SOLIDWORKS PART (.sldprt)
format: sldprt  version: not decoded by parser v0  size: 134,656 bytes
history: native  units: mm
features: plane x3, sketch x3, mirror x2, cut_extrude x2, material x1, extrude x1, fillet x1 (+13 scaffold rows collapsed)
feature tree (26):
  scaffold x13  (default folders/planes/origin — collapsed)
  material  "Material <nicht festgelegt>"
  plane  "Ebene vorne"
  plane  "Ebene oben"
  plane  "Ebene rechts"
  sketch  "Skizze1"  dims[c1.D1=150.0mm c1.D2=150.0mm c1.D3=~7.799541mm c2.D2=75.0mm]
  extrude  "Linear austragen1"  Depth=10mm
  fillet  "Verrundung1"  Radius=20mm
  mirror  "Spiegeln2"
  sketch  "Skizze3"  dims[c1.D1=5.0mm c1.D2=5.0mm c1.D3=20.0mm c1.D4=70.0mm c2.D1=30.0mm c2.D2=10.0mm c2.D3=70.0mm c2.D4=60.0mm]
  cut_extrude  "Schnitt-Linear austragen1"  [1 undecoded]
  mirror  "Verrundung2"
  sketch  "Skizze4"  dims[c1.D2=3.0mm c1.D1=6.0mm c2.D2=3.0mm c2.D3=50.0mm c2.D4=11.0mm]
  cut_extrude  "Schnitt-Linear austragen2"  Depth=10mm
decode coverage: 6 of 9 modeling features carry decoded parameters
note: ~ marks probable driven/reference dimensions
note: 1 parameter value undecoded
note: suppression state not decoded; provenance and decode notes live in map.json
